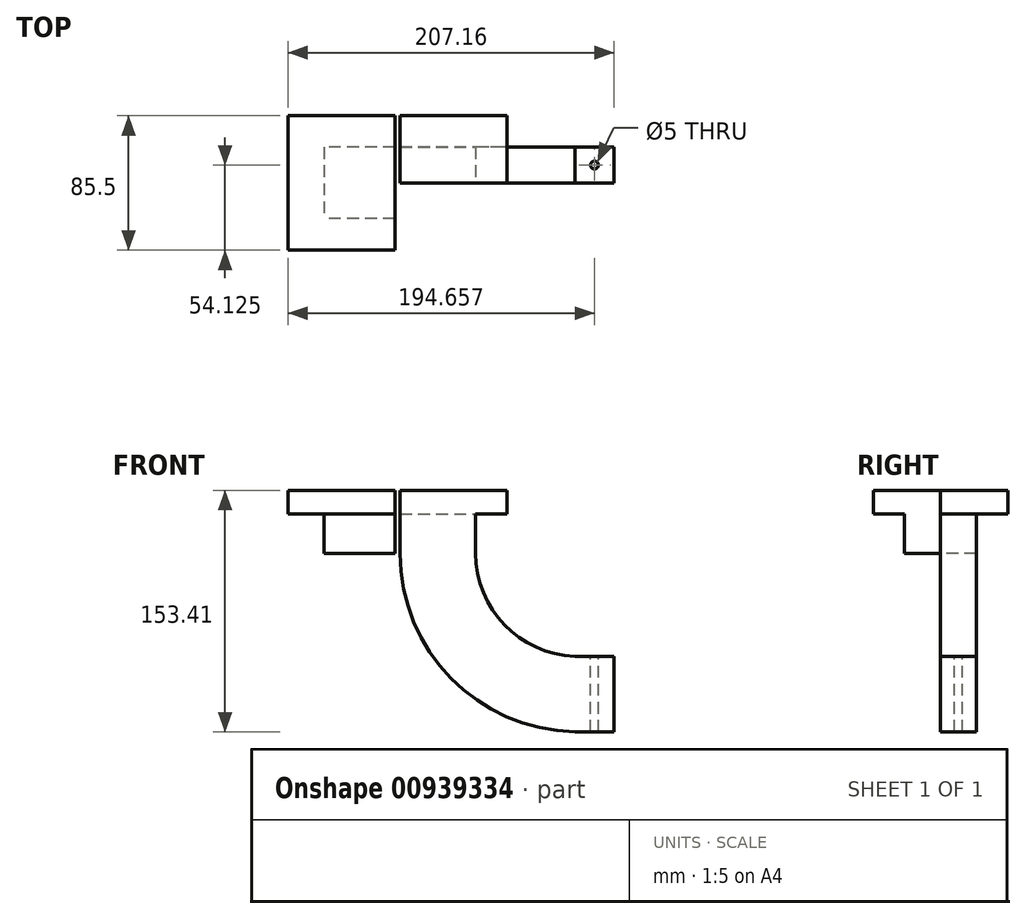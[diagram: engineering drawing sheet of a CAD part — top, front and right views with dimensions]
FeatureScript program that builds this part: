
annotation { "Feature Type Name" : "Feature", "Feature Type Description" : "" }
export const myFeature = defineFeature(function(context is Context, id is Id, definition is map)
    precondition{}
    {
        {
            var Q0;
            Q0=qCreatedBy(makeId("Top.planeOp"),FACE);
            var sketch = newSketch(context, id + "F0", { "sketchPlane" : qUnion([Q0])});
            skLineSegment(sketch, "E0.bottom", {"start": v(0, 22.75) * mm, "end": v(-45, 22.75) * mm});
            skLineSegment(sketch, "E0.top", {"start": v(0, -22.75) * mm, "end": v(-45, -22.75) * mm});
            skLineSegment(sketch, "E0.left", {"start": v(0, 22.75) * mm, "end": v(0, -22.75) * mm});
            skLineSegment(sketch, "E0.right", {"start": v(-45, 22.75) * mm, "end": v(-45, -22.75) * mm});
            skLineSegment(sketch, "E1.bottom", {"start": v(3.14, 22.75) * mm, "end": v(51.14, 22.75) * mm});
            skLineSegment(sketch, "E1.top", {"start": v(3.14, 0) * mm, "end": v(51.14, 0) * mm});
            skLineSegment(sketch, "E1.left", {"start": v(3.14, 22.75) * mm, "end": v(3.14, 0) * mm});
            skLineSegment(sketch, "E1.right", {"start": v(51.14, 22.75) * mm, "end": v(51.14, 0) * mm});
            skSolve(sketch);
        }
        {
            var Q0;
            Q0 = qSketchRegion(id + "F0", true);
            extrude(context, id + "F1", {"entities" : qUnion([Q0]), "depth" : 25 * mm, "offsetDistance" : 25 * mm});
        }
        {
            var Q0;
            Q0=makeQuery(id+"F1.opExtrude","CAP_FACE",FACE,{"disambiguationData":[OSD([sQuery(id+"F0.wireOp",EDGE,"E0.bottom"),sQuery(id+"F0.wireOp",EDGE,"E0.top"),sQuery(id+"F0.wireOp",EDGE,"E0.left"),sQuery(id+"F0.wireOp",EDGE,"E0.right")])],"isStart":false});
            var sketch = newSketch(context, id + "F2", { "sketchPlane" : qUnion([Q0])});
            skLineSegment(sketch, "E2.bottom", {"start": v(0, 42.75) * mm, "end": v(-68, 42.75) * mm});
            skLineSegment(sketch, "E2.top", {"start": v(0, -42.75) * mm, "end": v(-68, -42.75) * mm});
            skLineSegment(sketch, "E2.left", {"start": v(0, 42.75) * mm, "end": v(0, -42.75) * mm});
            skLineSegment(sketch, "E2.right", {"start": v(-68, 42.75) * mm, "end": v(-68, -42.75) * mm});
            skSolve(sketch);
        }
        {
            var Q0;
            Q0 = qSketchRegion(id + "F2", true);
            extrude(context, id + "F3", {"entities" : qUnion([Q0]), "operationType" : NewBodyOperationType.ADD, "depth" : 15 * mm, "offsetDistance" : 25 * mm});
        }
        {
            var Q0;
            Q0=makeQuery(id+"F1.opExtrude","CAP_FACE",FACE,{"disambiguationData":[OSD([sQuery(id+"F0.wireOp",EDGE,"E1.bottom"),sQuery(id+"F0.wireOp",EDGE,"E1.top"),sQuery(id+"F0.wireOp",EDGE,"E1.left"),sQuery(id+"F0.wireOp",EDGE,"E1.right")])],"isStart":false});
            var sketch = newSketch(context, id + "F4", { "sketchPlane" : qUnion([Q0])});
            skLineSegment(sketch, "E3.top", {"start": v(3.14, 42.75) * mm, "end": v(71.14, 42.75) * mm});
            skLineSegment(sketch, "E4", {"start": v(3.14, 42.75) * mm, "end": v(3.14, 0) * mm});
            skLineSegment(sketch, "E5", {"start": v(71.14, 0) * mm, "end": v(71.14, 42.75) * mm});
            skLineSegment(sketch, "E6", {"start": v(71.14, 0) * mm, "end": v(3.14, 0) * mm});
            skSolve(sketch);
        }
        {
            var Q0;
            Q0 = qSketchRegion(id + "F4", true);
            extrude(context, id + "F5", {"entities" : qUnion([Q0]), "operationType" : NewBodyOperationType.ADD, "depth" : 15 * mm, "offsetDistance" : 25 * mm});
        }
        {
            var Q0;
            Q0=makeQuery(id+"F1.opExtrude","SWEPT_FACE",FACE,{"disambiguationData":[OSD([sQuery(id+"F0.wireOp",EDGE,"E1.bottom")])]});
            var sketch = newSketch(context, id + "F6", { "sketchPlane" : qUnion([Q0])});
            skArc(sketch, "E7", {"start": v(-114.16, -65.41) * mm, "mid": v(-69.45, -45.42) * mm, "end": v(-51.14, 0) * mm});
            skLineSegment(sketch, "E8", {"start": v(-51.14, 0) * mm, "end": v(-3.14, 0) * mm});
            skLineSegment(sketch, "E9", {"start": v(-114.16, -65.41) * mm, "end": v(-114.16, -113.41) * mm});
            skArc(sketch, "E10", {"start": v(-114.16, -113.41) * mm, "mid": v(-35.51, -79.35) * mm, "end": v(-3.14, 0) * mm});
            skLineSegment(sketch, "E11", {"start": v(-114.16, -65.41) * mm, "end": v(-139.16, -65.41) * mm});
            skLineSegment(sketch, "E12", {"start": v(-139.16, -65.41) * mm, "end": v(-139.16, -113.41) * mm});
            skLineSegment(sketch, "E13", {"start": v(-114.16, -113.41) * mm, "end": v(-139.16, -113.41) * mm});
            skSolve(sketch);
        }
        {
            var Q0;
            Q0 = qSketchRegion(id + "F6", true);
            extrude(context, id + "F7", {"entities" : qUnion([Q0]), "operationType" : NewBodyOperationType.ADD, "oppositeDirection" : true, "depth" : 22.75 * mm, "offsetDistance" : 25 * mm});
        }
        {
            var Q0;
            Q0=makeQuery(id+"F7.opExtrude","SWEPT_FACE",FACE,{"disambiguationData":[OSD([sQuery(id+"F6.wireOp",EDGE,"E11")])]});
            var sketch = newSketch(context, id + "F8", { "sketchPlane" : qUnion([Q0])});
            skPoint(sketch, "E14", {"position": v(126.66, 11.38) * mm});
            skPoint(sketch, "E14.positionSnap0", {"position": v(139.16, 11.38) * mm});
            skPoint(sketch, "E14.positionSnap1", {"position": v(126.66, 22.75) * mm});
            skSolve(sketch);
        }
        {
            var Q0;
            Q0=sQuery(id+"F8.wireOp",VERTEX,"E14");
            var Q1;
            Q1=makeQuery(id+"F1.opExtrude","SWEPT_BODY",BODY,{"disambiguationData":[OSD([sQuery(id+"F0.wireOp",EDGE,"E1.bottom"),sQuery(id+"F0.wireOp",EDGE,"E1.top"),sQuery(id+"F0.wireOp",EDGE,"E1.left"),sQuery(id+"F0.wireOp",EDGE,"E1.right")])]});
            hole(context, id + "F9", {"style" : HoleStyle.SIMPLE, "endStyle" : HoleEndStyle.THROUGH, "standardTappedOrClearance" : lookupTablePath({ "fit" : "Normal", "standard" : "ISO", "size" : "M4.5", "type" : "Clearance" }), "standardBlindInLast" : lookupTablePath({ "fit" : "Normal", "standard" : "ISO", "engagement" : "75%", "pitch" : "0.5 mm", "size" : "M4.5", "type" : "Clearance & tapped" }), "holeDiameter" : 5 * mm, "majorDiameter" : 5 * mm, "isTappedThrough" : true, "tappedDepth" : 12 * mm, "tapClearance" : 3, "locations" : qUnion([Q0]), "scope" : qUnion([Q1])});
        }
    });
